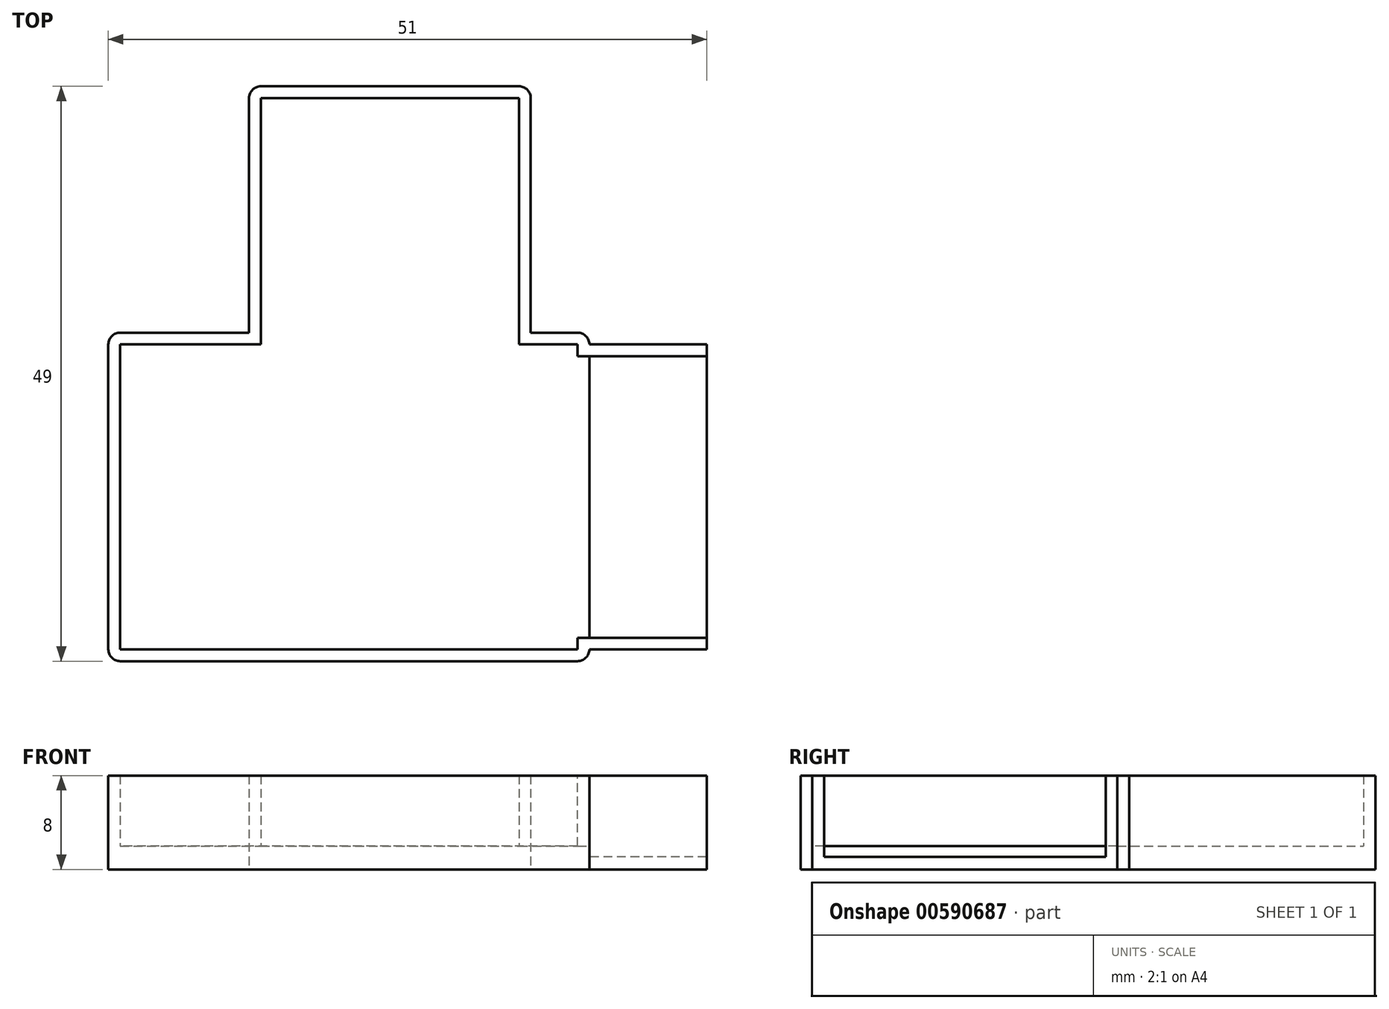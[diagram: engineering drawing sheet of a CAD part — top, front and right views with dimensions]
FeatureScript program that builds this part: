
annotation { "Feature Type Name" : "Feature", "Feature Type Description" : "" }
export const myFeature = defineFeature(function(context is Context, id is Id, definition is map)
    precondition{}
    {
        {
            var Q0;
            Q0=qCreatedBy(makeId("Top.planeOp"),FACE);
            var sketch = newSketch(context, id + "F0", { "sketchPlane" : qUnion([Q0])});
            skLineSegment(sketch, "E0.top", {"start": v(-24, -28) * mm, "end": v(17, -28) * mm});
            skLineSegment(sketch, "E0.left", {"start": v(-24, 0) * mm, "end": v(-24, -28) * mm});
            skLineSegment(sketch, "E0.right", {"start": v(17, 0) * mm, "end": v(17, -28) * mm});
            skLineSegment(sketch, "E1.top", {"start": v(-12, 21) * mm, "end": v(12, 21) * mm});
            skLineSegment(sketch, "E1.left", {"start": v(-12, 0) * mm, "end": v(-12, 21) * mm});
            skLineSegment(sketch, "E1.right", {"start": v(12, 0) * mm, "end": v(12, 21) * mm});
            skLineSegment(sketch, "E2", {"start": v(12, 0) * mm, "end": v(17, 0) * mm});
            skLineSegment(sketch, "E3", {"start": v(-12, 0) * mm, "end": v(-24, 0) * mm});
            skSolve(sketch);
        }
        {
            var Q0;
            Q0 = qSketchRegion(id + "F0", true);
            extrude(context, id + "F1", {"entities" : qUnion([Q0]), "depth" : 2 * mm, "offsetDistance" : 25 * mm});
        }
        {
            var Q0;
            Q0=makeQuery(id+"F1.opExtrude","CAP_FACE",FACE,{"disambiguationData":[OSD([sQuery(id+"F0.wireOp",EDGE,"E0.top"),sQuery(id+"F0.wireOp",EDGE,"E0.left"),sQuery(id+"F0.wireOp",EDGE,"E0.right"),sQuery(id+"F0.wireOp",EDGE,"E1.top"),sQuery(id+"F0.wireOp",EDGE,"E1.left"),sQuery(id+"F0.wireOp",EDGE,"E1.right"),sQuery(id+"F0.wireOp",EDGE,"E2"),sQuery(id+"F0.wireOp",EDGE,"E3")])],"isStart":false});
            var sketch = newSketch(context, id + "F2", { "sketchPlane" : qUnion([Q0])});
            skLineSegment(sketch, "E4", {"start": v(-11, -1) * mm, "end": v(-11, 20) * mm});
            skLineSegment(sketch, "E5", {"start": v(-11, 20) * mm, "end": v(11, 20) * mm});
            skLineSegment(sketch, "E6", {"start": v(11, 20) * mm, "end": v(11, -1) * mm});
            skLineSegment(sketch, "E7", {"start": v(11, -1) * mm, "end": v(16, -1) * mm});
            skLineSegment(sketch, "E8", {"start": v(16, -1) * mm, "end": v(16, -27) * mm});
            skLineSegment(sketch, "E9", {"start": v(16, -27) * mm, "end": v(-23, -27) * mm});
            skLineSegment(sketch, "E10", {"start": v(-23, -27) * mm, "end": v(-23, -1) * mm});
            skLineSegment(sketch, "E11", {"start": v(-23, -1) * mm, "end": v(-11, -1) * mm});
            skLineSegment(sketch, "E12", {"start": v(-24, -28) * mm, "end": v(-24, 0) * mm});
            skLineSegment(sketch, "E13", {"start": v(-24, 0) * mm, "end": v(-12, 0) * mm});
            skLineSegment(sketch, "E14", {"start": v(-12, 0) * mm, "end": v(-12, 21) * mm});
            skLineSegment(sketch, "E15", {"start": v(-12, 21) * mm, "end": v(12, 21) * mm});
            skLineSegment(sketch, "E16", {"start": v(12, 21) * mm, "end": v(12, 0) * mm});
            skLineSegment(sketch, "E17", {"start": v(12, 0) * mm, "end": v(17, 0) * mm});
            skLineSegment(sketch, "E18", {"start": v(17, 0) * mm, "end": v(17, -28) * mm});
            skLineSegment(sketch, "E19", {"start": v(17, -28) * mm, "end": v(-24, -28) * mm});
            skSolve(sketch);
        }
        {
            var Q0;
            Q0 = qSketchRegion(id + "F2", true);
            extrude(context, id + "F3", {"entities" : qUnion([Q0]), "operationType" : NewBodyOperationType.ADD, "depth" : 6 * mm, "offsetDistance" : 25 * mm});
        }
        {
            var Q0;
            Q0=makeQuery(id+"F3.boolean.opBoolean","MERGE",FACE,{"derivedFrom":[makeQuery(id+"F1.opExtrude","SWEPT_FACE",FACE,{"disambiguationData":[OSD([sQuery(id+"F0.wireOp",EDGE,"E0.right")])]}),makeQuery(id+"F3.opExtrude","SWEPT_FACE",FACE,{"disambiguationData":[OSD([sQuery(id+"F2.wireOp",EDGE,"E18")])]})]});
            var sketch = newSketch(context, id + "F4", { "sketchPlane" : qUnion([Q0])});
            skLineSegment(sketch, "E20.bottom", {"start": v(-26, 8) * mm, "end": v(-2, 8) * mm});
            skLineSegment(sketch, "E20.top", {"start": v(-26, 2) * mm, "end": v(-2, 2) * mm});
            skLineSegment(sketch, "E20.left", {"start": v(-26, 8) * mm, "end": v(-26, 2) * mm});
            skLineSegment(sketch, "E20.right", {"start": v(-2, 8) * mm, "end": v(-2, 2) * mm});
            skSolve(sketch);
        }
        {
            var Q0;
            Q0 = qSketchRegion(id + "F4", true);
            extrude(context, id + "F5", {"entities" : qUnion([Q0]), "operationType" : NewBodyOperationType.REMOVE, "endBound" : BoundingType.UP_TO_NEXT, "oppositeDirection" : true, "depth" : 1 * mm, "offsetDistance" : 25 * mm});
        }
        {
            var Q0;
            Q0=makeQuery(id+"F3.boolean.opBoolean","MERGE",EDGE,{"derivedFrom":[makeQuery(id+"F1.opExtrude","SWEPT_EDGE",EDGE,{"disambiguationData":[OSD([sQuery(id+"F0.wireOp",EDGE,"E0.left"),sQuery(id+"F0.wireOp",EDGE,"E3")])]}),makeQuery(id+"F3.opExtrude","SWEPT_EDGE",EDGE,{"disambiguationData":[OSD([sQuery(id+"F2.wireOp",EDGE,"E12"),sQuery(id+"F2.wireOp",EDGE,"E13")])]})]});
            var Q1;
            Q1=makeQuery(id+"F3.boolean.opBoolean","MERGE",EDGE,{"derivedFrom":[makeQuery(id+"F1.opExtrude","SWEPT_EDGE",EDGE,{"disambiguationData":[OSD([sQuery(id+"F0.wireOp",EDGE,"E1.top"),sQuery(id+"F0.wireOp",EDGE,"E1.left")])]}),makeQuery(id+"F3.opExtrude","SWEPT_EDGE",EDGE,{"disambiguationData":[OSD([sQuery(id+"F2.wireOp",EDGE,"E14"),sQuery(id+"F2.wireOp",EDGE,"E15")])]})]});
            var Q2;
            Q2=makeQuery(id+"F3.boolean.opBoolean","MERGE",EDGE,{"derivedFrom":[makeQuery(id+"F1.opExtrude","SWEPT_EDGE",EDGE,{"disambiguationData":[OSD([sQuery(id+"F0.wireOp",EDGE,"E1.top"),sQuery(id+"F0.wireOp",EDGE,"E1.right")])]}),makeQuery(id+"F3.opExtrude","SWEPT_EDGE",EDGE,{"disambiguationData":[OSD([sQuery(id+"F2.wireOp",EDGE,"E15"),sQuery(id+"F2.wireOp",EDGE,"E16")])]})]});
            var Q3;
            Q3=makeQuery(id+"F3.boolean.opBoolean","MERGE",EDGE,{"derivedFrom":[makeQuery(id+"F1.opExtrude","SWEPT_EDGE",EDGE,{"disambiguationData":[OSD([sQuery(id+"F0.wireOp",EDGE,"E0.right"),sQuery(id+"F0.wireOp",EDGE,"E2")])]}),makeQuery(id+"F3.opExtrude","SWEPT_EDGE",EDGE,{"disambiguationData":[OSD([sQuery(id+"F2.wireOp",EDGE,"E17"),sQuery(id+"F2.wireOp",EDGE,"E18")])]})]});
            var Q4;
            Q4=makeQuery(id+"F3.boolean.opBoolean","MERGE",EDGE,{"derivedFrom":[makeQuery(id+"F1.opExtrude","SWEPT_EDGE",EDGE,{"disambiguationData":[OSD([sQuery(id+"F0.wireOp",EDGE,"E0.top"),sQuery(id+"F0.wireOp",EDGE,"E0.right")])]}),makeQuery(id+"F3.opExtrude","SWEPT_EDGE",EDGE,{"disambiguationData":[OSD([sQuery(id+"F2.wireOp",EDGE,"E18"),sQuery(id+"F2.wireOp",EDGE,"E19")])]})]});
            var Q5;
            Q5=makeQuery(id+"F3.boolean.opBoolean","MERGE",EDGE,{"derivedFrom":[makeQuery(id+"F1.opExtrude","SWEPT_EDGE",EDGE,{"disambiguationData":[OSD([sQuery(id+"F0.wireOp",EDGE,"E0.top"),sQuery(id+"F0.wireOp",EDGE,"E0.left")])]}),makeQuery(id+"F3.opExtrude","SWEPT_EDGE",EDGE,{"disambiguationData":[OSD([sQuery(id+"F2.wireOp",EDGE,"E12"),sQuery(id+"F2.wireOp",EDGE,"E19")])]})]});
            fillet(context, id + "F6", {"entities" : qUnion([Q0, Q1, Q2, Q3, Q4, Q5]), "radius" : 1 * mm, "tangentPropagation" : true, "allowEdgeOverflow" : false});
        }
        {
            var Q0;
            Q0=makeQuery(id+"F3.boolean.opBoolean","MERGE",FACE,{"derivedFrom":[makeQuery(id+"F1.opExtrude","SWEPT_FACE",FACE,{"disambiguationData":[OSD([sQuery(id+"F0.wireOp",EDGE,"E0.right")])]}),makeQuery(id+"F3.opExtrude","SWEPT_FACE",FACE,{"disambiguationData":[OSD([sQuery(id+"F2.wireOp",EDGE,"E18")])]})]});
            var sketch = newSketch(context, id + "F7", { "sketchPlane" : qUnion([Q0])});
            skLineSegment(sketch, "E21.0", {"start": v(-26, 8) * mm, "end": v(-26, 2) * mm});
            skLineSegment(sketch, "E21.1", {"start": v(-2, 8) * mm, "end": v(-2, 2) * mm});
            skLineSegment(sketch, "E22", {"start": v(-26, 1.07) * mm, "end": v(-2, 1.07) * mm});
            skLineSegment(sketch, "E23", {"start": v(-2, 1.07) * mm, "end": v(-2, 2) * mm});
            skLineSegment(sketch, "E24", {"start": v(-26, 1.07) * mm, "end": v(-26, 2) * mm});
            skLineSegment(sketch, "E25", {"start": v(-26, 8) * mm, "end": v(-27, 8) * mm});
            skLineSegment(sketch, "E26", {"start": v(-27, 8) * mm, "end": v(-27, 0) * mm});
            skLineSegment(sketch, "E27", {"start": v(-27, 0) * mm, "end": v(-1, 0) * mm});
            skLineSegment(sketch, "E28", {"start": v(-1, 0) * mm, "end": v(-1, 8) * mm});
            skLineSegment(sketch, "E29", {"start": v(-1, 8) * mm, "end": v(-2, 8) * mm});
            skSolve(sketch);
        }
        {
            var Q0;
            Q0 = qSketchRegion(id + "F7", true);
            extrude(context, id + "F8", {"entities" : qUnion([Q0]), "operationType" : NewBodyOperationType.ADD, "depth" : 10 * mm, "offsetDistance" : 25 * mm});
        }
    });
